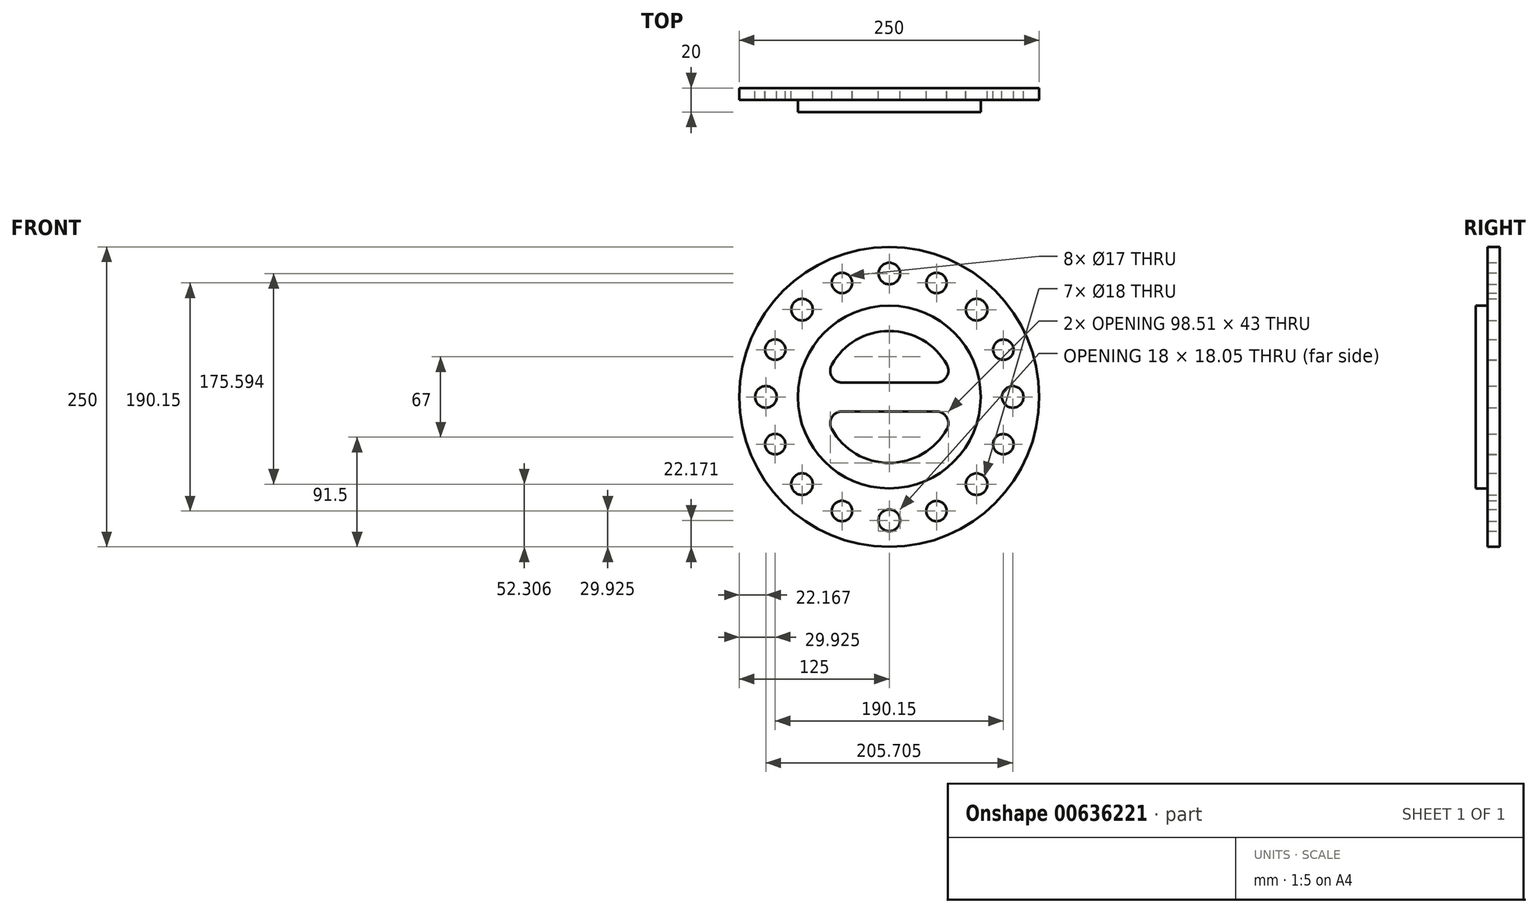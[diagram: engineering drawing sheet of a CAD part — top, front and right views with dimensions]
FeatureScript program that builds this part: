
annotation { "Feature Type Name" : "Feature", "Feature Type Description" : "" }
export const myFeature = defineFeature(function(context is Context, id is Id, definition is map)
    precondition{}
    {
        {
            var Q0;
            Q0=qCreatedBy(makeId("Front.planeOp"),FACE);
            var sketch = newSketch(context, id + "F0", { "sketchPlane" : qUnion([Q0])});
            skCircle(sketch, "E0", {"center": v(0, 0) * mm, "radius": 125 * mm});
            skCircle(sketch, "E1", {"center": v(0, 0) * mm, "radius": 76.2 * mm});
            skCircle(sketch, "E2", {"center": v(0, -102.8) * mm, "radius": 9 * mm});
            skCircle(sketch, "E3.2.0", {"center": v(0, -102.85) * mm, "radius": 9 * mm});
            skCircle(sketch, "E3.3.0", {"center": v(0, -102.85) * mm, "radius": 9 * mm});
            skCircle(sketch, "E4.1.0", {"center": v(72.73, -72.7) * mm, "radius": 9 * mm});
            skCircle(sketch, "E4.2.0", {"center": v(102.87, 0.03) * mm, "radius": 9 * mm});
            skCircle(sketch, "E4.3.0", {"center": v(72.76, 72.76) * mm, "radius": 9 * mm});
            skCircle(sketch, "E4.4.0", {"center": v(0.04, 102.9) * mm, "radius": 9 * mm});
            skCircle(sketch, "E4.5.0", {"center": v(-72.7, 72.79) * mm, "radius": 9 * mm});
            skCircle(sketch, "E4.6.0", {"center": v(-102.83, 0.07) * mm, "radius": 9 * mm});
            skCircle(sketch, "E4.7.0", {"center": v(-72.72, -72.67) * mm, "radius": 9 * mm});
            skPoint(sketch, "E4.center", {"position": v(0.02, 0.05) * mm});
            skArc(sketch, "E5", {"start": v(0.04, 102.9) * mm, "mid": v(39.4, 95.06) * mm, "end": v(72.76, 72.76) * mm});
            skCircle(sketch, "E6", {"center": v(39.4, 95.06) * mm, "radius": 8.5 * mm});
            skCircle(sketch, "E7.1.0", {"center": v(-39.36, 95.07) * mm, "radius": 8.5 * mm});
            skCircle(sketch, "E7.2.0", {"center": v(-95.06, 39.4) * mm, "radius": 8.5 * mm});
            skCircle(sketch, "E7.3.0", {"center": v(-95.07, -39.36) * mm, "radius": 8.5 * mm});
            skCircle(sketch, "E7.4.0", {"center": v(-39.4, -95.06) * mm, "radius": 8.5 * mm});
            skCircle(sketch, "E7.5.0", {"center": v(39.36, -95.07) * mm, "radius": 8.5 * mm});
            skCircle(sketch, "E7.6.0", {"center": v(95.06, -39.4) * mm, "radius": 8.5 * mm});
            skCircle(sketch, "E7.7.0", {"center": v(95.07, 39.36) * mm, "radius": 8.5 * mm});
            skSolve(sketch);
        }
        {
            var Q0;
            Q0 = qSketchRegion(id + "F0", true);
            extrude(context, id + "F1", {"entities" : qUnion([Q0]), "depth" : 10 * mm, "offsetDistance" : 25 * mm});
        }
        {
            var Q0;
            Q0=qCreatedBy(makeId("Front.planeOp"),FACE);
            var sketch = newSketch(context, id + "F2", { "sketchPlane" : qUnion([Q0])});
            skCircle(sketch, "E8", {"center": v(0, 0) * mm, "radius": 76.2 * mm});
            skSolve(sketch);
        }
        {
            var Q0;
            Q0 = qSketchRegion(id + "F2", true);
            extrude(context, id + "F3", {"entities" : qUnion([Q0]), "operationType" : NewBodyOperationType.ADD, "depth" : 20 * mm, "offsetDistance" : 25 * mm});
        }
        {
            var Q0;
            Q0=makeQuery(id+"F3.opExtrude","CAP_FACE",FACE,{"disambiguationData":[OSD([sQuery(id+"F2.wireOp",EDGE,"E8")])],"isStart":false});
            var sketch = newSketch(context, id + "F4", { "sketchPlane" : qUnion([Q0])});
            skArc(sketch, "E9", {"start": v(-47.98, -26.89) * mm, "mid": v(0, -55) * mm, "end": v(47.98, -26.89) * mm});
            skLineSegment(sketch, "E10", {"start": v(-39.26, 12) * mm, "end": v(39.26, 12) * mm});
            skLineSegment(sketch, "E11", {"start": v(-39.26, -12) * mm, "end": v(39.26, -12) * mm});
            skArc(sketch, "E12.trimOffspring", {"start": v(47.98, 26.89) * mm, "mid": v(0, 55) * mm, "end": v(-47.98, 26.89) * mm});
            skPoint(sketch, "E13.visualSharp", {"position": v(-53.67, 12) * mm});
            skArc(sketch, "E13.filletArc", {"start": v(-47.98, 26.89) * mm, "mid": v(-47.88, 16.94) * mm, "end": v(-39.26, 12) * mm});
            skPoint(sketch, "E14.visualSharp", {"position": v(53.67, 12) * mm});
            skArc(sketch, "E14.filletArc", {"start": v(39.26, 12) * mm, "mid": v(47.88, 16.94) * mm, "end": v(47.98, 26.89) * mm});
            skPoint(sketch, "E15.visualSharp", {"position": v(-53.67, -12) * mm});
            skArc(sketch, "E15.filletArc", {"start": v(-39.26, -12) * mm, "mid": v(-47.88, -16.94) * mm, "end": v(-47.98, -26.89) * mm});
            skPoint(sketch, "E16.visualSharp", {"position": v(53.67, -12) * mm});
            skArc(sketch, "E16.filletArc", {"start": v(47.98, -26.89) * mm, "mid": v(47.88, -16.94) * mm, "end": v(39.26, -12) * mm});
            skSolve(sketch);
        }
        {
            var Q0;
            Q0=makeQuery(id+"F4.imprint","IMPRINT",FACE,{"disambiguationData":[TD([[makeQuery(id+"F4.imprint","IMPRINT",EDGE,{"derivedFrom":sQuery(id+"F4.wireOp",EDGE,"E10")}),1.0]])]});
            var Q1;
            Q1=makeQuery(id+"F4.imprint","IMPRINT",FACE,{"disambiguationData":[TD([[makeQuery(id+"F4.imprint","IMPRINT",EDGE,{"derivedFrom":sQuery(id+"F4.wireOp",EDGE,"E9")}),1.0]])]});
            extrude(context, id + "F5", {"entities" : qUnion([Q0, Q1]), "operationType" : NewBodyOperationType.REMOVE, "oppositeDirection" : true, "depth" : 25 * mm, "offsetDistance" : 25 * mm});
        }
    });
